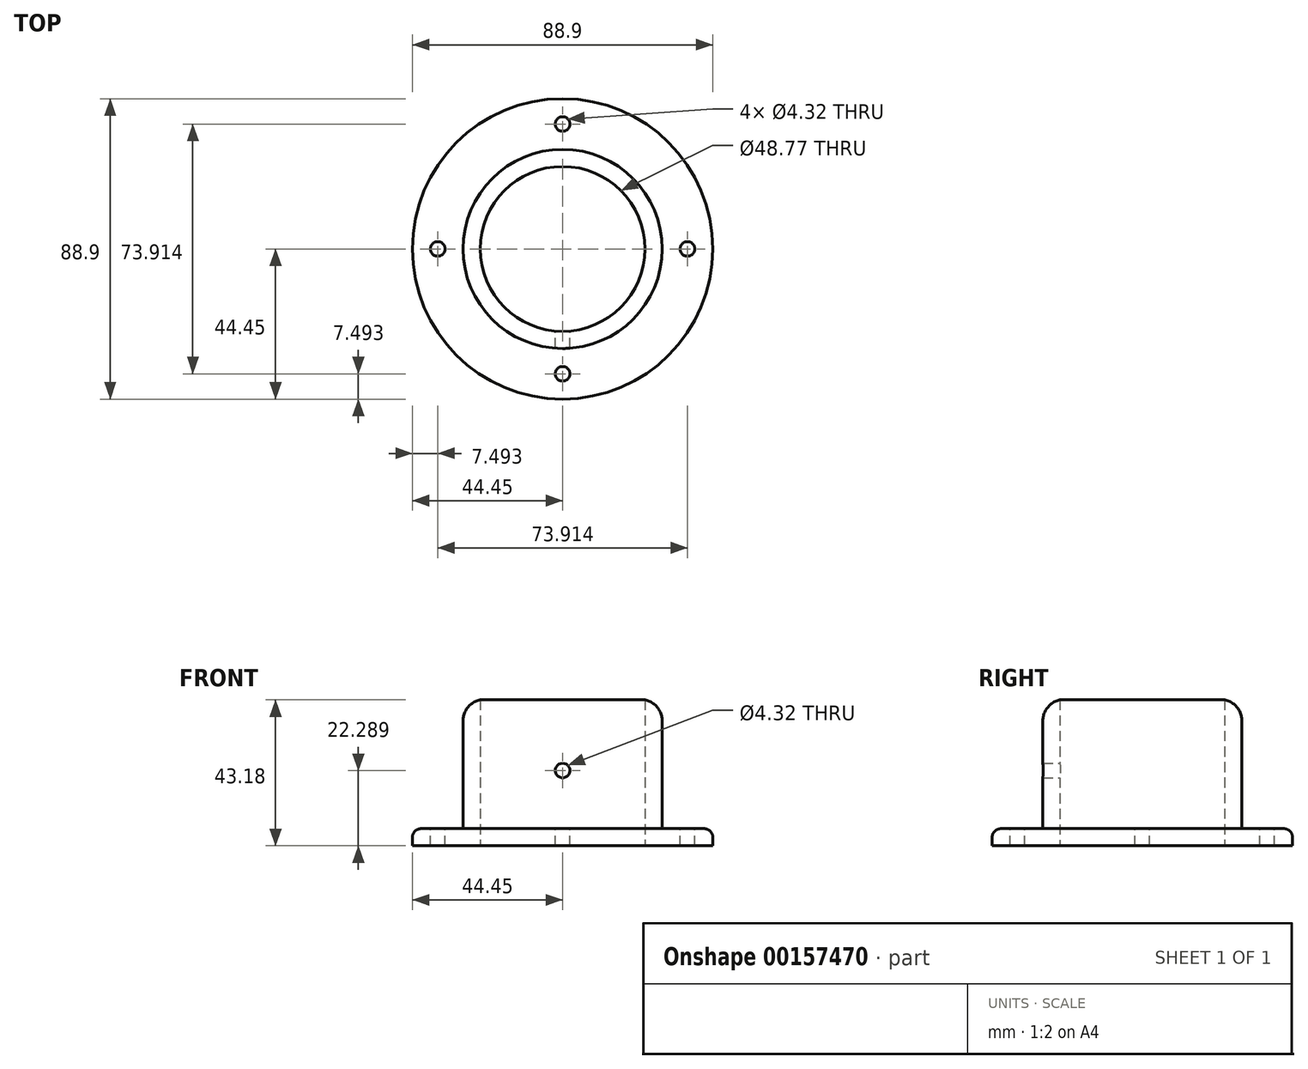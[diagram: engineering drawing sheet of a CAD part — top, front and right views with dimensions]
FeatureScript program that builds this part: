
annotation { "Feature Type Name" : "Feature", "Feature Type Description" : "" }
export const myFeature = defineFeature(function(context is Context, id is Id, definition is map)
    precondition{}
    {
        {
            var Q0;
            Q0=qCreatedBy(makeId("Top.planeOp"),FACE);
            var sketch = newSketch(context, id + "F0", { "sketchPlane" : qUnion([Q0])});
            skCircle(sketch, "E0", {"center": v(0, 0) * mm, "radius": 24.38 * mm});
            skCircle(sketch, "E1", {"center": v(0, 0) * mm, "radius": 44.45 * mm});
            skSolve(sketch);
        }
        {
            var Q0;
            Q0 = qSketchRegion(id + "F0", true);
            extrude(context, id + "F1", {"entities" : qUnion([Q0]), "depth" : 5.08 * mm});
        }
        {
            var Q0;
            Q0=makeQuery(id+"F1.opExtrude","CAP_FACE",FACE,{"disambiguationData":[OSD([sQuery(id+"F0.wireOp",EDGE,"E0"),sQuery(id+"F0.wireOp",EDGE,"E1")])],"isStart":false});
            var sketch = newSketch(context, id + "F2", { "sketchPlane" : qUnion([Q0])});
            skCircle(sketch, "E2", {"center": v(0, 0) * mm, "radius": 24.38 * mm});
            skCircle(sketch, "E3", {"center": v(0, 0) * mm, "radius": 29.46 * mm});
            skLineSegment(sketch, "E4", {"start": v(24.38, 0) * mm, "end": v(29.46, 0) * mm, "construction": true});
            skSolve(sketch);
        }
        {
            var Q0;
            Q0 = qSketchRegion(id + "F2", true);
            extrude(context, id + "F3", {"entities" : qUnion([Q0]), "operationType" : NewBodyOperationType.ADD, "depth" : 38.1 * mm});
        }
        {
            var Q0;
            Q0=makeQuery(id+"F1.opExtrude","CAP_EDGE",EDGE,{"disambiguationData":[OSD([sQuery(id+"F0.wireOp",EDGE,"E1")])],"isStart":false});
            var Q1;
            Q1=makeQuery(id+"F3.opExtrude","CAP_EDGE",EDGE,{"disambiguationData":[OSD([sQuery(id+"F2.wireOp",EDGE,"E3")])],"isStart":true});
            fillet(context, id + "F4", {"entities" : qUnion([Q0, Q1]), "radius" : 2.54 * mm, "tangentPropagation" : true, "allowEdgeOverflow" : false});
        }
        {
            var Q0;
            Q0=makeQuery(id+"F3.opExtrude","CAP_EDGE",EDGE,{"disambiguationData":[OSD([sQuery(id+"F2.wireOp",EDGE,"E3")])],"isStart":false});
            fillet(context, id + "F5", {"entities" : qUnion([Q0]), "radius" : 6.35 * mm, "tangentPropagation" : true, "allowEdgeOverflow" : false});
        }
        {
            var Q0;
            Q0=makeQuery(id+"F1.opExtrude","CAP_FACE",FACE,{"disambiguationData":[OSD([sQuery(id+"F0.wireOp",EDGE,"E0"),sQuery(id+"F0.wireOp",EDGE,"E1")])],"isStart":false});
            var sketch = newSketch(context, id + "F6", { "sketchPlane" : qUnion([Q0])});
            skCircle(sketch, "E5", {"center": v(-36.96, 0) * mm, "radius": 2.16 * mm});
            skCircle(sketch, "E6", {"center": v(0, 36.96) * mm, "radius": 2.16 * mm});
            skCircle(sketch, "E7", {"center": v(36.96, 0) * mm, "radius": 2.16 * mm});
            skCircle(sketch, "E8", {"center": v(0, -36.96) * mm, "radius": 2.16 * mm});
            skLineSegment(sketch, "E9", {"start": v(0, 41.91) * mm, "end": v(0, 32) * mm, "construction": true});
            skLineSegment(sketch, "E10", {"start": v(0, 0) * mm, "end": v(0, 36.96) * mm, "construction": true});
            skLineSegment(sketch, "E11", {"start": v(0, 0) * mm, "end": v(-36.96, 0) * mm, "construction": true});
            skLineSegment(sketch, "E12", {"start": v(0, 0) * mm, "end": v(0, -36.96) * mm, "construction": true});
            skLineSegment(sketch, "E13", {"start": v(0, 0) * mm, "end": v(36.96, 0) * mm, "construction": true});
            skSolve(sketch);
        }
        {
            var Q0;
            Q0 = qSketchRegion(id + "F6", true);
            var Q1;
            Q1=makeQuery(id+"F1.opExtrude","CAP_FACE",FACE,{"disambiguationData":[OSD([sQuery(id+"F0.wireOp",EDGE,"E0"),sQuery(id+"F0.wireOp",EDGE,"E1")])],"isStart":true});
            extrude(context, id + "F7", {"entities" : qUnion([Q0]), "operationType" : NewBodyOperationType.REMOVE, "endBound" : BoundingType.UP_TO_SURFACE, "oppositeDirection" : true, "endBoundEntityFace" : qUnion([Q1]), "depth" : 25.4 * mm});
        }
        {
            var Q0;
            Q0=qCreatedBy(makeId("Front.planeOp"),FACE);
            var sketch = newSketch(context, id + "F8", { "sketchPlane" : qUnion([Q0])});
            skCircle(sketch, "E14", {"center": v(0, 22.29) * mm, "radius": 2.16 * mm});
            skLineSegment(sketch, "E15", {"start": v(0, 7.62) * mm, "end": v(0, 36.96) * mm, "construction": true});
            skSolve(sketch);
        }
        {
            var Q0;
            Q0 = qSketchRegion(id + "F8", true);
            var Q1;
            Q1=makeQuery(id+"F3.opExtrude","SWEPT_FACE",FACE,{"disambiguationData":[OSD([sQuery(id+"F2.wireOp",EDGE,"E3")])]});
            extrude(context, id + "F9", {"entities" : qUnion([Q0]), "operationType" : NewBodyOperationType.REMOVE, "endBound" : BoundingType.UP_TO_SURFACE, "endBoundEntityFace" : qUnion([Q1]), "depth" : 25.4 * mm});
        }
        {
            var Q0;
            Q0=qCreatedBy(makeId("Front.planeOp"),FACE);
            var sketch = newSketch(context, id + "F10", { "sketchPlane" : qUnion([Q0])});
            skLineSegment(sketch, "E16", {"start": v(0, 0) * mm, "end": v(0, 43.18) * mm, "construction": true});
            skSolve(sketch);
        }
    });
